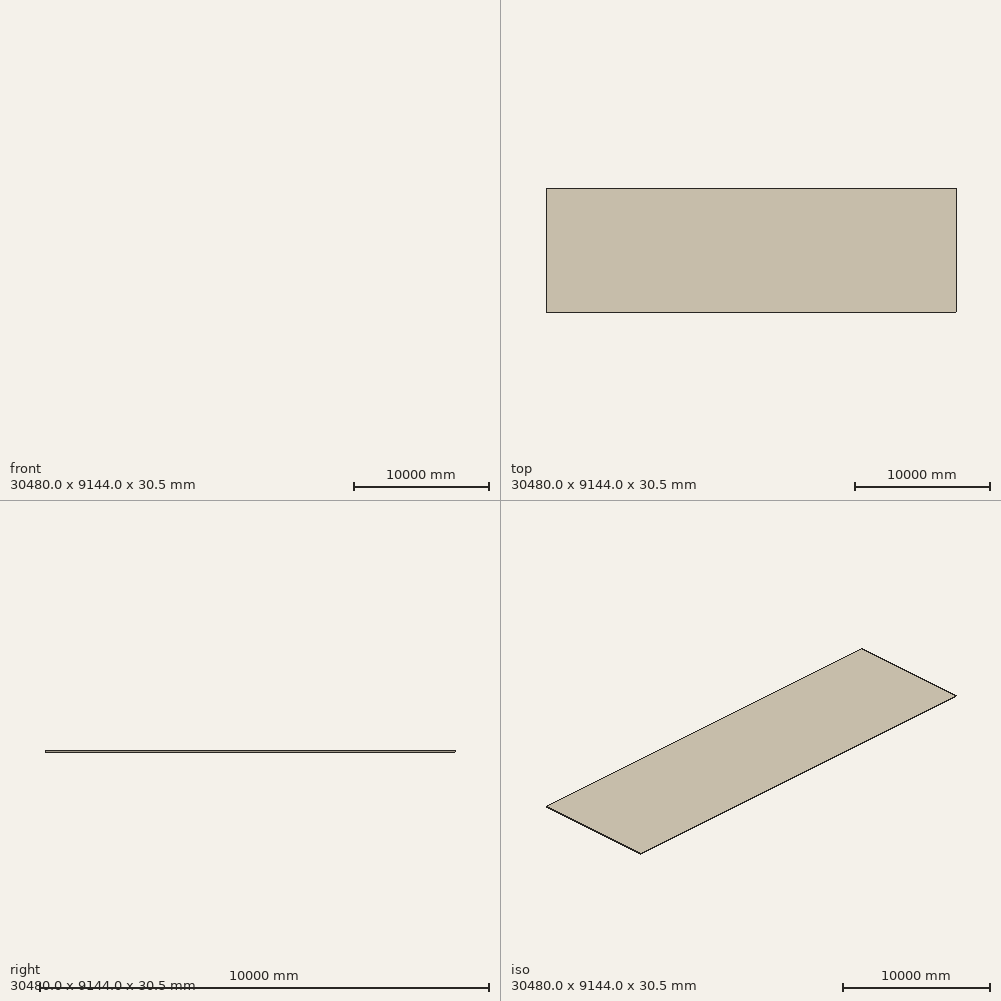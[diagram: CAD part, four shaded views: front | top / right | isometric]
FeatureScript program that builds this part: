
annotation { "Feature Type Name" : "Feature", "Feature Type Description" : "" }
export const myFeature = defineFeature(function(context is Context, id is Id, definition is map)
    precondition{}
    {
        {
            var Q0;
            Q0=qCreatedBy(makeId("Top.planeOp"),FACE);
            var sketch = newSketch(context, id + "F0", { "sketchPlane" : qUnion([Q0])});
            skLineSegment(sketch, "E0.bottom", {"start": v(15240, -4572) * mm, "end": v(-15240, -4572) * mm});
            skLineSegment(sketch, "E0.top", {"start": v(15240, 4572) * mm, "end": v(-15240, 4572) * mm});
            skLineSegment(sketch, "E0.left", {"start": v(15240, -4572) * mm, "end": v(15240, 4572) * mm});
            skLineSegment(sketch, "E0.right", {"start": v(-15240, -4572) * mm, "end": v(-15240, 4572) * mm});
            skPoint(sketch, "E0.middle", {"position": v(0, 0) * mm});
            skSolve(sketch);
        }
        {
            var Q0;
            Q0=makeQuery(id+"F0.imprint","IMPRINT",FACE,{"disambiguationData":[TD([[makeQuery(id+"F0.imprint","IMPRINT",EDGE,{"derivedFrom":sQuery(id+"F0.wireOp",EDGE,"E0.bottom")}),-1.0]])]});
            extrude(context, id + "F1", {"entities" : qUnion([Q0]), "depth" : 30.48 * mm});
        }
    });
